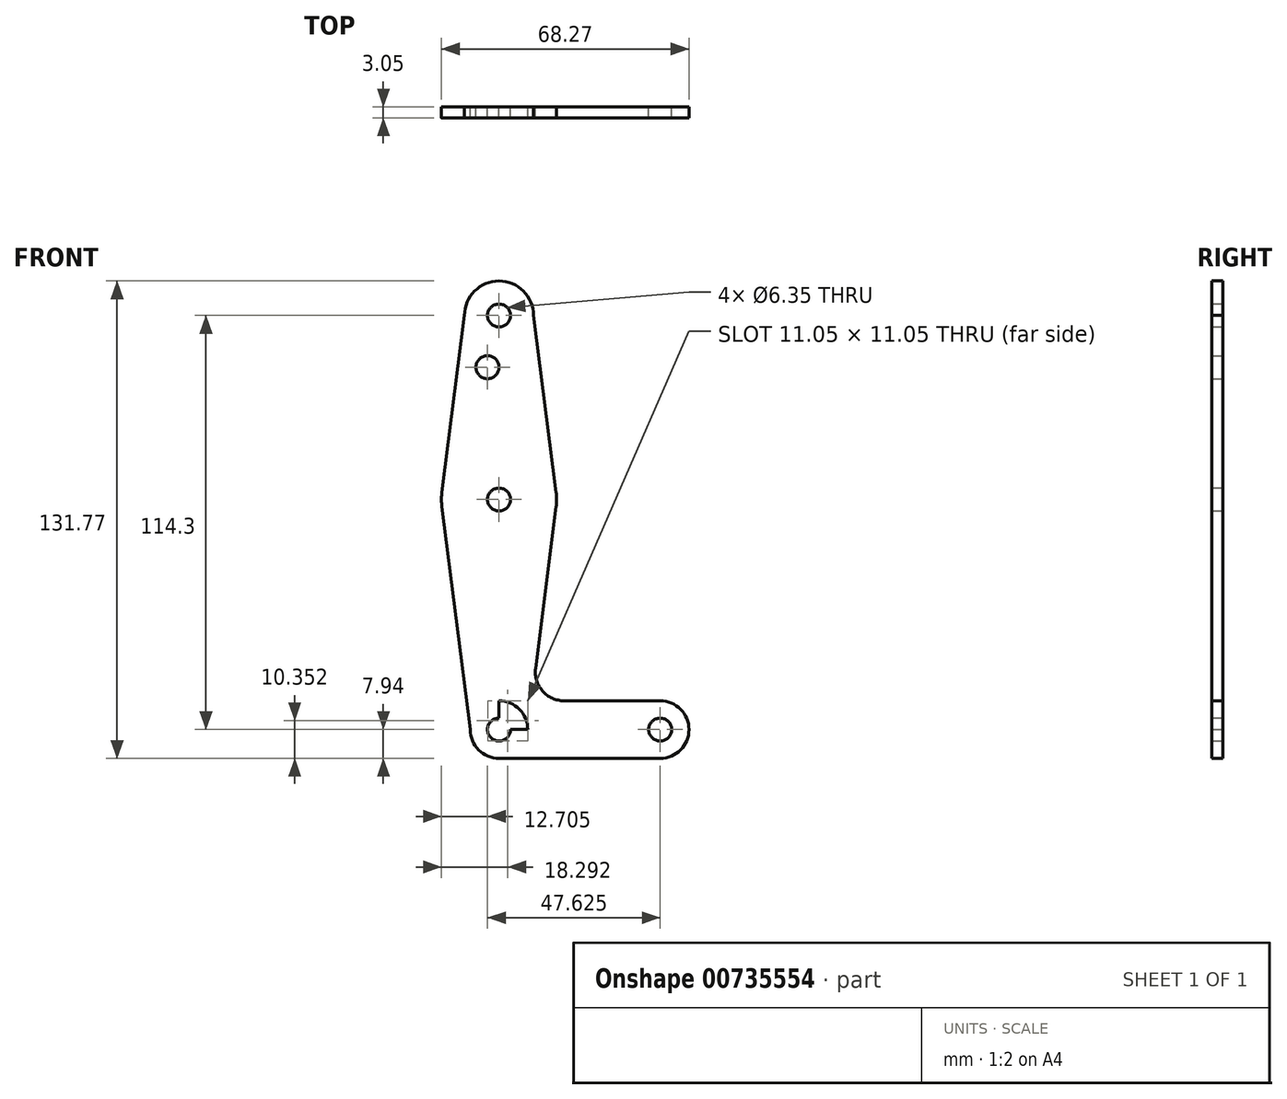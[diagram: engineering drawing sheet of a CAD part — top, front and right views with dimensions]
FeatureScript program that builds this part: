
annotation { "Feature Type Name" : "Feature", "Feature Type Description" : "" }
export const myFeature = defineFeature(function(context is Context, id is Id, definition is map)
    precondition{}
    {
        {
            var Q0;
            Q0=qCreatedBy(makeId("Front.planeOp"),FACE);
            var sketch = newSketch(context, id + "F0", { "sketchPlane" : qUnion([Q0])});
            skLineSegment(sketch, "E0", {"start": v(0, 0) * mm, "end": v(0, 114.3) * mm});
            skLineSegment(sketch, "E1", {"start": v(0, 0) * mm, "end": v(44.45, 0) * mm});
            skCircle(sketch, "E2", {"center": v(0, 114.3) * mm, "radius": 9.53 * mm});
            skCircle(sketch, "E3", {"center": v(0, 0) * mm, "radius": 7.94 * mm});
            skCircle(sketch, "E4", {"center": v(44.45, 0) * mm, "radius": 7.94 * mm});
            skCircle(sketch, "E5", {"center": v(0, 63.5) * mm, "radius": 15.88 * mm});
            skLineSegment(sketch, "E6", {"start": v(-9.53, 114.3) * mm, "end": v(-15.75, 65.5) * mm});
            skLineSegment(sketch, "E7", {"start": v(9.53, 114.3) * mm, "end": v(15.75, 65.5) * mm});
            skLineSegment(sketch, "E8", {"start": v(15.75, 61.5) * mm, "end": v(10.08, 16.89) * mm});
            skLineSegment(sketch, "E9", {"start": v(-15.75, 61.5) * mm, "end": v(-7.94, 0) * mm});
            skLineSegment(sketch, "E10", {"start": v(17.97, 7.94) * mm, "end": v(44.45, 7.94) * mm});
            skLineSegment(sketch, "E11", {"start": v(0, -7.94) * mm, "end": v(44.45, -7.94) * mm});
            skCircle(sketch, "E12", {"center": v(0, 114.3) * mm, "radius": 3.18 * mm});
            skCircle(sketch, "E13", {"center": v(0, 63.5) * mm, "radius": 3.18 * mm});
            skCircle(sketch, "E14", {"center": v(0, 0) * mm, "radius": 3.18 * mm});
            skCircle(sketch, "E15", {"center": v(44.45, 0) * mm, "radius": 3.18 * mm});
            skCircle(sketch, "E16", {"center": v(-3.18, 100.03) * mm, "radius": 3.18 * mm});
            skArc(sketch, "E17.filletArc", {"start": v(10.08, 16.89) * mm, "mid": v(12, 10.63) * mm, "end": v(17.97, 7.94) * mm});
            skSolve(sketch);
        }
        {
            var Q0;
            Q0 = qSketchRegion(id + "F0", true);
            extrude(context, id + "F1", {"entities" : qUnion([Q0]), "depth" : 3.05 * mm, "offsetDistance" : 25.4 * mm});
        }
    });
